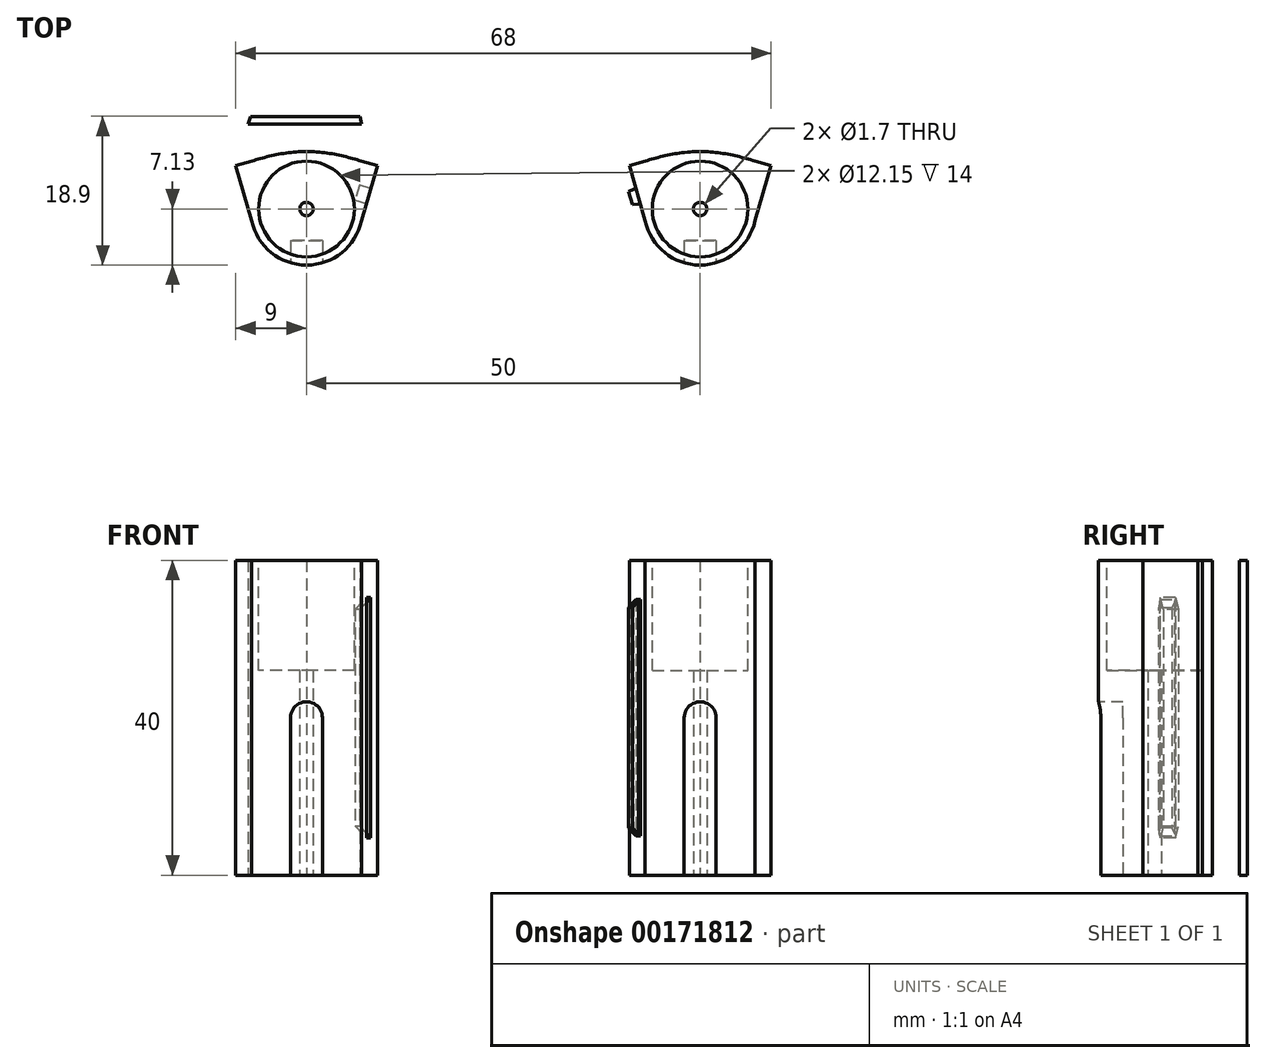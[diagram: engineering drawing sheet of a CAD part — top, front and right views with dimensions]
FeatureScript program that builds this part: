
annotation { "Feature Type Name" : "Feature", "Feature Type Description" : "" }
export const myFeature = defineFeature(function(context is Context, id is Id, definition is map)
    precondition{}
    {
        {
            var Q0;
            Q0=qCreatedBy(makeId("Top.planeOp"),FACE);
            var sketch = newSketch(context, id + "F0", { "sketchPlane" : qUnion([Q0])});
            skCircle(sketch, "E0", {"center": v(0, 0) * mm, "radius": 7.12 * mm});
            skFitSpline(sketch, "E1.MirrorCS", {"points": [v(-0.02, 7.3) * mm, v(6.94, 6.1) * mm], "startDerivative": vector(7.57, -0.03) * mm, "endDerivative": vector(5.81, -1.8) * mm});
            skCircle(sketch, "E2", {"center": v(0, 0) * mm, "radius": 0.85 * mm});
            skLineSegment(sketch, "E3", {"start": v(6.67, -2.5) * mm, "end": v(9, 5.5) * mm});
            skLineSegment(sketch, "E4", {"start": v(6.94, 6.1) * mm, "end": v(9, 5.5) * mm});
            skFitSpline(sketch, "E5.MirrorCS", {"points": [v(0.02, 7.3) * mm, v(-6.94, 6.1) * mm], "startDerivative": vector(-7.57, -0.03) * mm, "endDerivative": vector(-5.81, -1.8) * mm});
            skLineSegment(sketch, "E6.MirrorCS", {"start": v(-6.94, 6.1) * mm, "end": v(-9, 5.5) * mm});
            skLineSegment(sketch, "E7.MirrorCS", {"start": v(-6.67, -2.5) * mm, "end": v(-9, 5.5) * mm});
            skLineSegment(sketch, "E8.bottom", {"start": v(9, 5.5) * mm, "end": v(-9, 5.5) * mm, "construction": true});
            skLineSegment(sketch, "E8.top", {"start": v(9, -5.5) * mm, "end": v(-9, -5.5) * mm, "construction": true});
            skLineSegment(sketch, "E8.left", {"start": v(9, 5.5) * mm, "end": v(9, -5.5) * mm, "construction": true});
            skLineSegment(sketch, "E8.right", {"start": v(-9, 5.5) * mm, "end": v(-9, -5.5) * mm, "construction": true});
            skLineSegment(sketch, "E9.top", {"start": v(9, 6.1) * mm, "end": v(-9, 6.1) * mm, "construction": true});
            skLineSegment(sketch, "E9.left", {"start": v(9, 5.5) * mm, "end": v(9, 6.1) * mm, "construction": true});
            skLineSegment(sketch, "E9.right", {"start": v(-9, 5.5) * mm, "end": v(-9, 6.1) * mm, "construction": true});
            skLineSegment(sketch, "E10.bottom", {"start": v(-9, 6.1) * mm, "end": v(9, 6.1) * mm, "construction": true});
            skLineSegment(sketch, "E10.top", {"start": v(-9, 6.7) * mm, "end": v(9, 6.7) * mm, "construction": true});
            skLineSegment(sketch, "E10.left", {"start": v(-9, 6.1) * mm, "end": v(-9, 6.7) * mm, "construction": true});
            skLineSegment(sketch, "E10.right", {"start": v(9, 6.1) * mm, "end": v(9, 6.7) * mm, "construction": true});
            skLineSegment(sketch, "E11.bottom", {"start": v(9, 6.7) * mm, "end": v(-9, 6.7) * mm, "construction": true});
            skLineSegment(sketch, "E11.top", {"start": v(9, 7.3) * mm, "end": v(-9, 7.3) * mm, "construction": true});
            skLineSegment(sketch, "E11.left", {"start": v(9, 6.7) * mm, "end": v(9, 7.3) * mm, "construction": true});
            skLineSegment(sketch, "E11.right", {"start": v(-9, 6.7) * mm, "end": v(-9, 7.3) * mm, "construction": true});
            skLineSegment(sketch, "E12", {"start": v(-2.5, 7.3) * mm, "end": v(-2.5, -5.5) * mm, "construction": true});
            skLineSegment(sketch, "E13", {"start": v(-5, 7.3) * mm, "end": v(-5, -5.5) * mm, "construction": true});
            skLineSegment(sketch, "E14", {"start": v(-9, -2.5) * mm, "end": v(9, -2.5) * mm, "construction": true});
            skLineSegment(sketch, "E15", {"start": v(-9, 0) * mm, "end": v(9, 0) * mm, "construction": true});
            skSolve(sketch);
        }
        {
            var Q0;
            Q0 = qSketchRegion(id + "F0", true);
            extrude(context, id + "F1", {"entities" : qUnion([Q0]), "depth" : 40 * mm});
        }
        {
            var Q0;
            Q0=qCreatedBy(makeId("Right.planeOp"),FACE);
            cPlane(context, id + "F2", {"entities" : qUnion([Q0]), "cplaneType" : CPlaneType.OFFSET, "offset" : 25 * mm, "width" : 150 * mm, "height" : 150 * mm});
        }
        {
            var Q0;
            Q0=makeQuery(id+"F1.opExtrude","CAP_FACE",FACE,{"disambiguationData":[OSD([sQuery(id+"F0.wireOp",EDGE,"E0"),sQuery(id+"F0.wireOp",EDGE,"33f2417f-aedc-4336-9c77-3ec6a05d2b9b"),sQuery(id+"F0.wireOp",EDGE,"0b92c4b9-511d-4a65-8099-57b238cdf4ca"),sQuery(id+"F0.wireOp",EDGE,"E1.MirrorCS"),sQuery(id+"F0.wireOp",EDGE,"5a11bc20-f998-4e9e-9fb4-e6cc9914e4070.MirrorCS")])],"isStart":false});
            var sketch = newSketch(context, id + "F3", { "sketchPlane" : qUnion([Q0])});
            skCircle(sketch, "E16", {"center": v(0, 0) * mm, "radius": 6.08 * mm});
            skSolve(sketch);
        }
        {
            var Q0;
            Q0 = qSketchRegion(id + "F3", true);
            extrude(context, id + "F4", {"entities" : qUnion([Q0]), "operationType" : NewBodyOperationType.REMOVE, "oppositeDirection" : true, "depth" : 14 * mm});
        }
        {
            var Q0;
            Q0=qCreatedBy(makeId("Top.planeOp"),FACE);
            var sketch = newSketch(context, id + "F5", { "sketchPlane" : qUnion([Q0])});
            skLineSegment(sketch, "E17.bottom", {"start": v(-7.43, 11.77) * mm, "end": v(7.03, 11.77) * mm});
            skLineSegment(sketch, "E17.top", {"start": v(-7.43, 10.78) * mm, "end": v(7.03, 10.78) * mm});
            skLineSegment(sketch, "E18", {"start": v(-7.43, 10.78) * mm, "end": v(-6.04, 14.62) * mm});
            skLineSegment(sketch, "E19", {"start": v(7.03, 10.78) * mm, "end": v(6.07, 14.62) * mm});
            skSolve(sketch);
        }
        {
            var Q0;
            {var subQ5=sQuery(id+"F5.wireOp",EDGE,"E17.top");Q0=makeQuery(id+"F5.imprint","IMPRINT",FACE,{"disambiguationData":[TD([[makeQuery(id+"F5.imprint","IMPRINT",EDGE,{"derivedFrom":subQ5}),1.0]])]});}
            extrude(context, id + "F6", {"entities" : qUnion([Q0]), "depth" : 40 * mm});
        }
        {
            var Q0;
            Q0=qCreatedBy(makeId("Front.planeOp"),FACE);
            cPlane(context, id + "F7", {"entities" : qUnion([Q0]), "cplaneType" : CPlaneType.OFFSET, "offset" : 10 * mm, "width" : 150 * mm, "height" : 150 * mm});
        }
        {
            var Q0;
            Q0=qCreatedBy(id+"F7.planeOp",FACE);
            var sketch = newSketch(context, id + "F8", { "sketchPlane" : qUnion([Q0])});
            skLineSegment(sketch, "E20.top", {"start": v(-2.03, 0) * mm, "end": v(2.03, 0) * mm});
            skLineSegment(sketch, "E20.left", {"start": v(-2.03, 20) * mm, "end": v(-2.03, 0) * mm});
            skLineSegment(sketch, "E20.right", {"start": v(2.03, 20) * mm, "end": v(2.03, 0) * mm});
            skArc(sketch, "E21", {"start": v(-2.03, 20) * mm, "mid": v(0, 22.03) * mm, "end": v(2.03, 20) * mm});
            skSolve(sketch);
        }
        {
            var Q0;
            Q0 = qSketchRegion(id + "F8", true);
            extrude(context, id + "F9", {"entities" : qUnion([Q0]), "operationType" : NewBodyOperationType.REMOVE, "oppositeDirection" : true, "depth" : 6 * mm});
        }
        {
            var Q0;
            Q0=makeQuery(id+"F1.opExtrude","SWEPT_BODY",BODY,{"disambiguationData":[OSD([sQuery(id+"F0.wireOp",EDGE,"E0"),sQuery(id+"F0.wireOp",EDGE,"33f2417f-aedc-4336-9c77-3ec6a05d2b9b"),sQuery(id+"F0.wireOp",EDGE,"0b92c4b9-511d-4a65-8099-57b238cdf4ca"),sQuery(id+"F0.wireOp",EDGE,"E1.MirrorCS"),sQuery(id+"F0.wireOp",EDGE,"E2"),sQuery(id+"F0.wireOp",EDGE,"7746a3c4-c509-4acf-8033-0175272c69fa"),sQuery(id+"F0.wireOp",EDGE,"E3")])]});
            var Q1;
            Q1=qCreatedBy(id+"F2.planeOp",FACE);
            mirror(context, id + "F10", {"entities" : qUnion([Q0]), "mirrorPlane" : qUnion([Q1])});
        }
        {
            var Q0;
            Q0=makeQuery(id+"F10.opPattern","COPY",FACE,{"derivedFrom":makeQuery(id+"F1.opExtrude","SWEPT_FACE",FACE,{"disambiguationData":[OSD([sQuery(id+"F0.wireOp",EDGE,"E3")])]}),"instanceName":"1"});
            var sketch = newSketch(context, id + "F11", { "sketchPlane" : qUnion([Q0])});
            skLineSegment(sketch, "E22.bottom", {"start": v(11.17, 35) * mm, "end": v(9.17, 35) * mm});
            skLineSegment(sketch, "E22.top", {"start": v(11.17, 5) * mm, "end": v(9.17, 5) * mm});
            skLineSegment(sketch, "E22.left", {"start": v(11.17, 35) * mm, "end": v(11.17, 5) * mm});
            skLineSegment(sketch, "E22.right", {"start": v(9.17, 35) * mm, "end": v(9.17, 5) * mm});
            skPoint(sketch, "E22.middle", {"position": v(10.17, 20) * mm});
            skSolve(sketch);
        }
        {
            var Q0;
            Q0=makeQuery(id+"F1.opExtrude","SWEPT_FACE",FACE,{"disambiguationData":[OSD([sQuery(id+"F0.wireOp",EDGE,"E3")])]});
            var sketch = newSketch(context, id + "F12", { "sketchPlane" : qUnion([Q0])});
            skLineSegment(sketch, "E23.bottom", {"start": v(4.8, 35.25) * mm, "end": v(2.8, 35.25) * mm});
            skLineSegment(sketch, "E23.top", {"start": v(4.8, 4.75) * mm, "end": v(2.8, 4.75) * mm});
            skLineSegment(sketch, "E23.left", {"start": v(4.8, 35.25) * mm, "end": v(4.8, 4.75) * mm});
            skLineSegment(sketch, "E23.right", {"start": v(2.8, 35.25) * mm, "end": v(2.8, 4.75) * mm});
            skPoint(sketch, "E23.middle", {"position": v(3.8, 20) * mm});
            skSolve(sketch);
        }
        {
            var Q0;
            Q0 = qSketchRegion(id + "F11", true);
            extrude(context, id + "F13", {"entities" : qUnion([Q0]), "operationType" : NewBodyOperationType.ADD, "depth" : 1 * mm});
        }
        {
            var Q0;
            Q0 = qSketchRegion(id + "F12", true);
            extrude(context, id + "F14", {"entities" : qUnion([Q0]), "operationType" : NewBodyOperationType.REMOVE, "oppositeDirection" : true, "depth" : 1.5 * mm});
        }
        {
            var Q0;
            Q0=makeQuery(id+"F13.opExtrude","CAP_EDGE",EDGE,{"disambiguationData":[OSD([sQuery(id+"F11.wireOp",EDGE,"E22.top")])],"isStart":false});
            var Q1;
            Q1=makeQuery(id+"F13.opExtrude","CAP_EDGE",EDGE,{"disambiguationData":[OSD([sQuery(id+"F11.wireOp",EDGE,"E22.bottom")])],"isStart":false});
            chamfer(context, id + "F15", {"entities" : qUnion([Q0, Q1]), "width" : 1 * mm, "tangentPropagation" : true});
        }
        {
            var Q0;
            Q0=makeQuery(id+"F13.opExtrude","CAP_EDGE",EDGE,{"disambiguationData":[OSD([sQuery(id+"F11.wireOp",EDGE,"E22.left")])],"isStart":false});
            var Q1;
            Q1=makeQuery(id+"F13.opExtrude","CAP_EDGE",EDGE,{"disambiguationData":[OSD([sQuery(id+"F11.wireOp",EDGE,"E22.right")])],"isStart":false});
            chamfer(context, id + "F16", {"entities" : qUnion([Q0, Q1]), "chamferType" : ChamferType.OFFSET_ANGLE, "width" : 0.75 * mm, "oppositeDirection" : false, "angle" : 10 * degree, "tangentPropagation" : true});
        }
        {
            var Q0;
            Q0=makeQuery(id+"F14.boolean.opBoolean","COPY",EDGE,{"derivedFrom":makeQuery(id+"F14.opExtrude","CAP_EDGE",EDGE,{"disambiguationData":[OSD([sQuery(id+"F12.wireOp",EDGE,"E23.bottom")])],"isStart":false})});
            var Q1;
            Q1=makeQuery(id+"F14.boolean.opBoolean","COPY",EDGE,{"derivedFrom":makeQuery(id+"F14.opExtrude","CAP_EDGE",EDGE,{"disambiguationData":[OSD([sQuery(id+"F12.wireOp",EDGE,"E23.top")])],"isStart":false})});
            chamfer(context, id + "F17", {"entities" : qUnion([Q0, Q1]), "width" : 1.5 * mm, "tangentPropagation" : true});
        }
    });
